# Revit family: Sink-Topmount-Acorn-SD-2522-80_Series
name_source: partatom
category: Plumbing Fixtures
units: mm (PartAtom-declared; Revit-internal decimal feet)

## family parameters
Cut with Voids When Loaded = No
Host = Face
OmniClass Number = 23.45.05.14.14
OmniClass Title = Sinks/Lavatories
Part Type = Normal
Room Calculation Point = No
Round Connector Dimension = Use Diameter
Shared = Yes

## types (8) — shared parameters
Assembly Code = D2010440
Bowl Length = 15 3/4"
Bowl Width = 21"
CW Connection = No
CWFU = 3
Compliance Certifications = ASME A112.19.3/CSA B45.4, IAPMO® Certified
Default Elevation = 34"
Description = Stainless Steel Drop In Sink
Drain Opening Size = 3 1/2"
Finish = Stainless Steel-Acorn-Satin
HW Connection = No
HWFU = 3
Height = 8"
Installation Type = Wall Mounted
Left Faucet Hole2 Distance = 8"
Length = 22"
Manufacturer = Acorn
Material = Stainless Steel-Acorn-Satin
Product Page URL = https://www.acorneng.com
Revised Date = 07/08/2024
Right Faucet Hole2 Distance = 8"
URL = https://www.acorneng.com
Vent Connection = No
WFU = 4
Waste Connection = No
Width = 25"

## per-type parameters (varying)
| type | -0 Blank, No Deck Punching | -1 Single Hole Centered | -2 2 Holes on 4” Centers (4” Centerset) | -2R Single Hole Centered w/ 2nd Hole 4” to Right | -3 3 Holes on 4” Centers (8” Centerset) | -4L 3 Holes on 4” Centers w/ 4th Hole 4” to Left | -4R 3 Holes on 4” Centers w/ 4th Hole 4” to Right | -5 5 Holes on 4” Centers | Central Faucet Hole Depth | Left Faucet Hole Depth | Left Faucet Hole Distance | Left Faucet Hole2 Depth | Right Faucet Hole Depth | Right Faucet Hole Distance | Right Faucet Hole2 Depth |
| SD-2220-80-0 | Yes | No | No | No | No | No | No | No | 1" | 1" | 4" | 1" | 1" | 4" | 1" |
| SD-2220-80-1 | No | Yes | No | No | No | No | No | No | 2" | 1" | 4" | 1" | 1" | 4" | 1" |
| SD-2220-80-2R | No | No | No | Yes | No | No | No | No | 2" | 1" | 4" | 1" | 2" | 4" | 1" |
| SD-2220-80-2 | No | No | Yes | No | No | No | No | No | 1" | 2" | 2" | 1" | 2" | 2" | 1" |
| SD-2220-80-3 | No | No | No | No | Yes | No | No | No | 2" | 2" | 4" | 1" | 2" | 4" | 1" |
| SD-2220-80-4L | No | No | No | No | No | Yes | No | No | 2" | 2" | 4" | 2" | 2" | 4" | 1" |
| SD-2220-80-4R | No | No | No | No | No | No | Yes | No | 2" | 2" | 4" | 1" | 2" | 4" | 2" |
| SD-2220-80-5 | No | No | No | No | No | No | No | Yes | 2" | 2" | 4" | 2" | 2" | 4" | 2" |

note: column(s) folded — value = type name in every type: Model

## geometry (parser evidence)
native form markers: Sweep x3
no freeform markers — native parametric forms only
